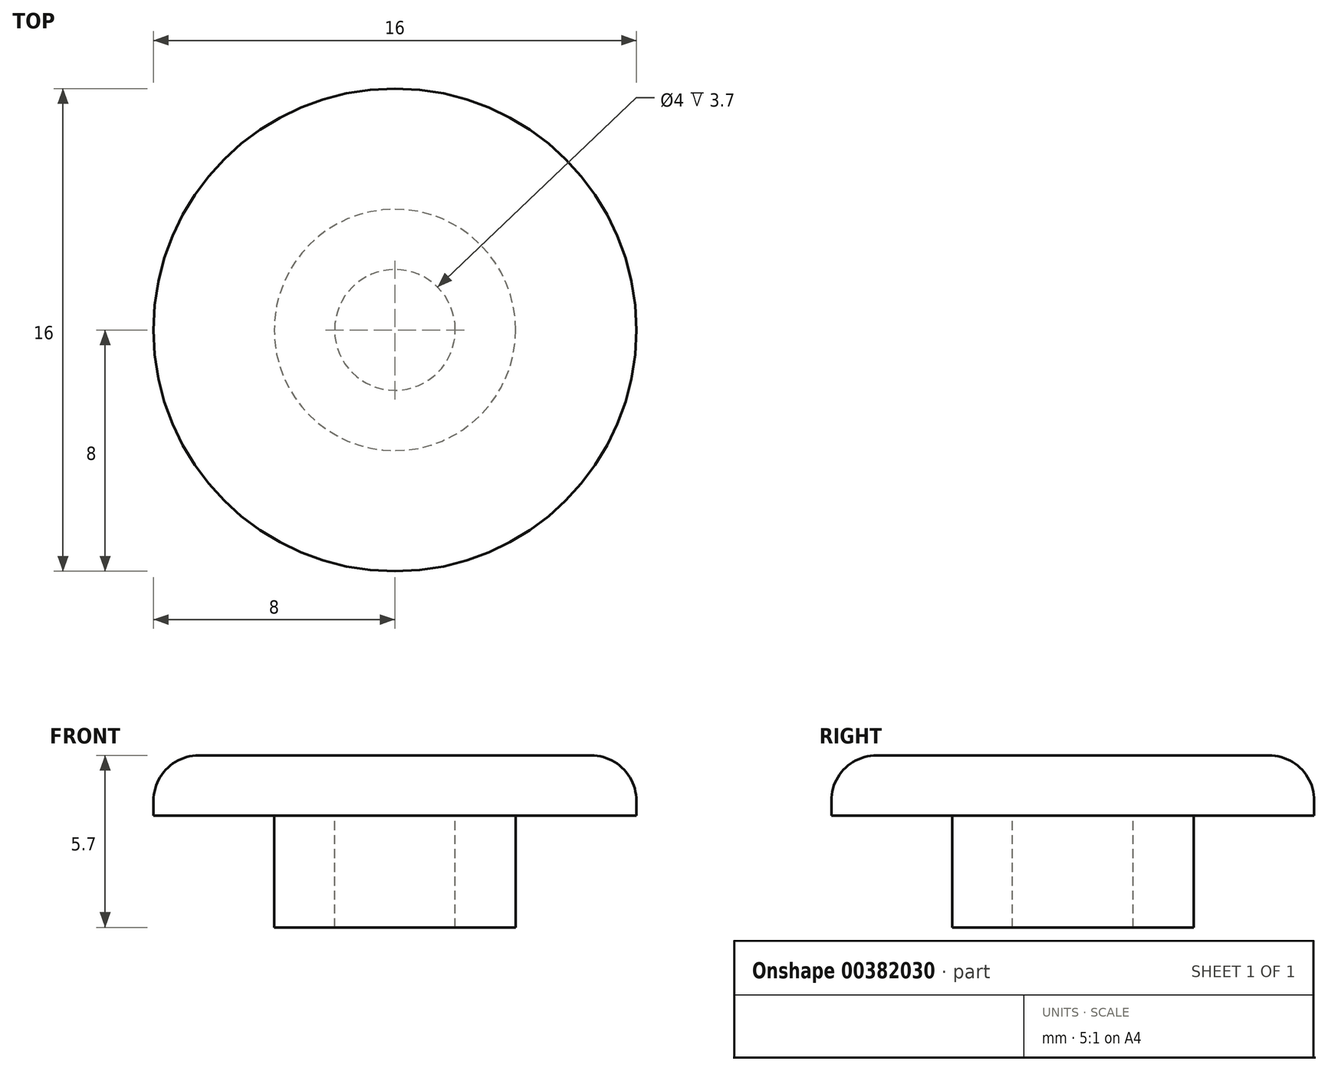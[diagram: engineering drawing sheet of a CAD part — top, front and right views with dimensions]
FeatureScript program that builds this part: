
annotation { "Feature Type Name" : "Feature", "Feature Type Description" : "" }
export const myFeature = defineFeature(function(context is Context, id is Id, definition is map)
    precondition{}
    {
        {
            var Q0;
            Q0=qCreatedBy(makeId("Top.planeOp"),FACE);
            var sketch = newSketch(context, id + "F0", { "sketchPlane" : qUnion([Q0])});
            skCircle(sketch, "E0", {"center": v(0, 0) * mm, "radius": 8 * mm});
            skCircle(sketch, "E1", {"center": v(0, 0) * mm, "radius": 4 * mm});
            skCircle(sketch, "E2", {"center": v(0, 0) * mm, "radius": 2 * mm});
            skSolve(sketch);
        }
        {
            var Q0;
            Q0=qSketchRegion(id+"F0",true);
            var Q1;
            Q1=makeQuery(id+"F0.imprint","IMPRINT",FACE,{"disambiguationData":[TD([[makeQuery(id+"F0.imprint","IMPRINT",EDGE,{"derivedFrom":sQuery(id+"F0.wireOp",EDGE,"E1")}),1.0]])]});
            var Q2;
            Q2=makeQuery(id+"F0.imprint","IMPRINT",FACE,{"disambiguationData":[TD([[makeQuery(id+"F0.imprint","IMPRINT",EDGE,{"derivedFrom":sQuery(id+"F0.wireOp",EDGE,"E2")}),1.0]])]});
            extrude(context, id + "F1", {"entities" : qUnion([Q0, Q1, Q2]), "depth" : 2 * mm});
        }
        {
            var Q0;
            Q0=makeQuery(id+"F0.imprint","IMPRINT",FACE,{"disambiguationData":[TD([[makeQuery(id+"F0.imprint","IMPRINT",EDGE,{"derivedFrom":sQuery(id+"F0.wireOp",EDGE,"E1")}),1.0]])]});
            extrude(context, id + "F2", {"entities" : qUnion([Q0]), "operationType" : NewBodyOperationType.ADD, "depth" : -3.7 * mm});
        }
        {
            var Q0;
            Q0=makeQuery(id+"F1.opExtrude","CAP_EDGE",EDGE,{"disambiguationData":[OSD([sQuery(id+"F0.wireOp",EDGE,"E0")])],"isStart":false});
            fillet(context, id + "F3", {"entities" : qUnion([Q0]), "radius" : 1.5 * mm, "tangentPropagation" : true, "allowEdgeOverflow" : false});
        }
    });
